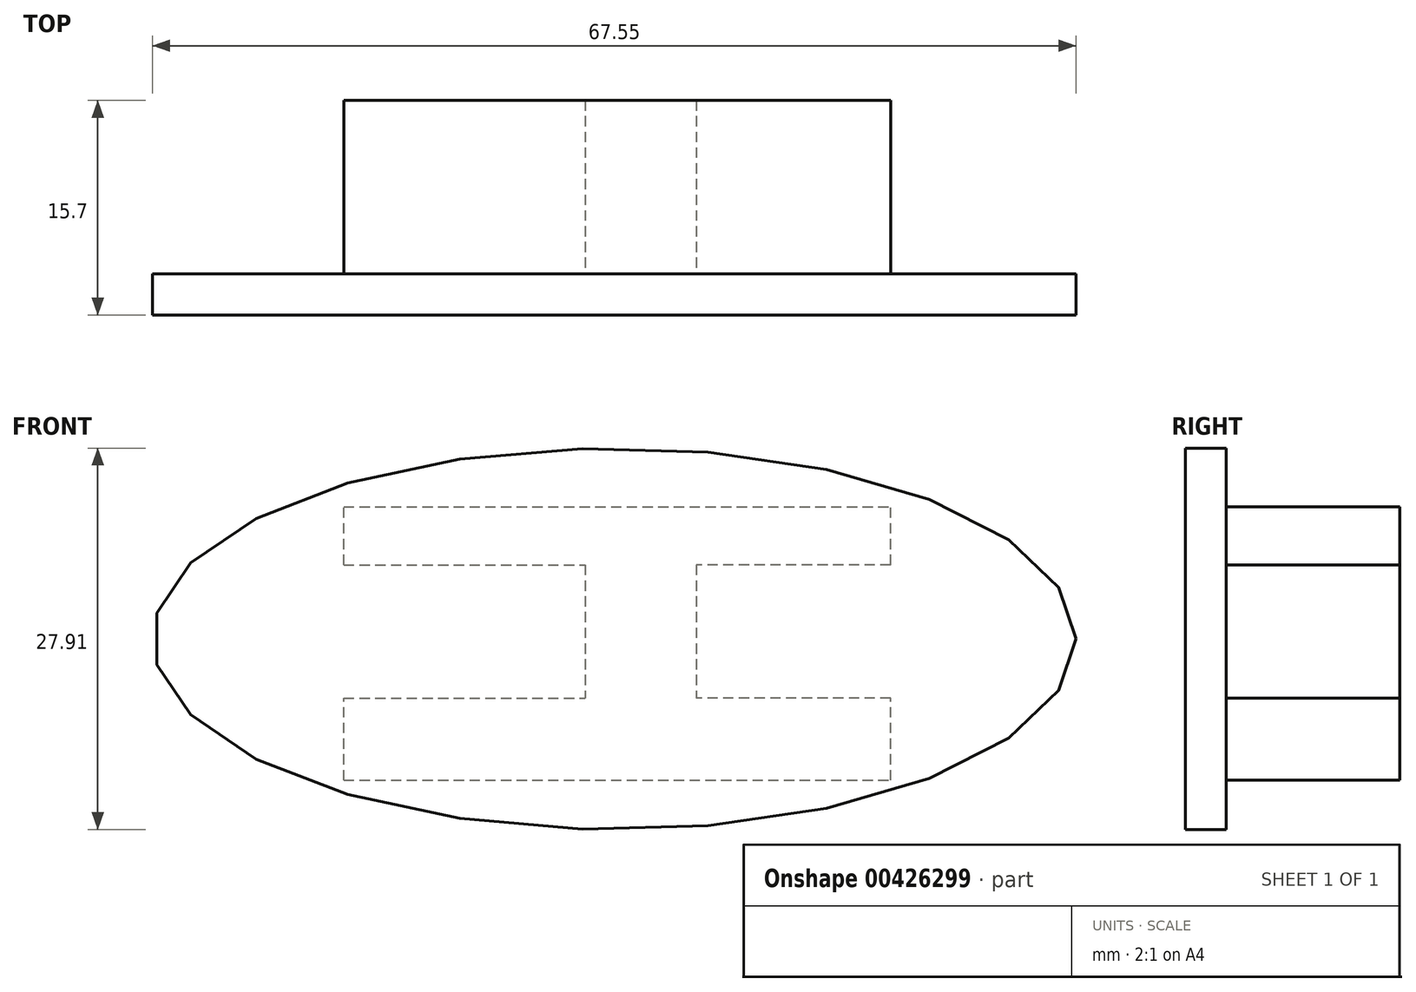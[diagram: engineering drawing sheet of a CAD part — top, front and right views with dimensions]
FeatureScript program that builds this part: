
annotation { "Feature Type Name" : "Feature", "Feature Type Description" : "" }
export const myFeature = defineFeature(function(context is Context, id is Id, definition is map)
    precondition{}
    {
        {
            var Q0;
            Q0=qCreatedBy(makeId("Front.planeOp"),FACE);
            var sketch = newSketch(context, id + "F0", { "sketchPlane" : qUnion([Q0])});
            skLineSegment(sketch, "E0.bottom", {"start": v(0, 0) * mm, "end": v(40, 0) * mm});
            skLineSegment(sketch, "E0.top", {"start": v(0, 20) * mm, "end": v(40, 20) * mm});
            skLineSegment(sketch, "E0.left", {"start": v(0, 0) * mm, "end": v(0, 6.02) * mm});
            skLineSegment(sketch, "E0.right", {"start": v(40, 0) * mm, "end": v(40, 6.02) * mm});
            skLineSegment(sketch, "E1.bottom", {"start": v(0, 15.76) * mm, "end": v(17.67, 15.76) * mm});
            skLineSegment(sketch, "E1.top", {"start": v(0, 6.02) * mm, "end": v(17.67, 6.02) * mm});
            skLineSegment(sketch, "E1.right", {"start": v(17.67, 15.76) * mm, "end": v(17.67, 6.02) * mm});
            skLineSegment(sketch, "E2.bottom", {"start": v(40, 15.76) * mm, "end": v(25.78, 15.76) * mm});
            skLineSegment(sketch, "E2.top", {"start": v(40, 6.02) * mm, "end": v(25.78, 6.02) * mm});
            skLineSegment(sketch, "E2.right", {"start": v(25.78, 15.76) * mm, "end": v(25.78, 6.02) * mm});
            skLineSegment(sketch, "E3.trimOffspring", {"start": v(0, 15.76) * mm, "end": v(0, 20) * mm});
            skLineSegment(sketch, "E4.trimOffspring", {"start": v(40, 15.76) * mm, "end": v(40, 20) * mm});
            skSolve(sketch);
        }
        {
            var Q0;
            Q0 = qSketchRegion(id + "F0", true);
            extrude(context, id + "F1", {"entities" : qUnion([Q0]), "oppositeDirection" : true, "depth" : 12.7 * mm});
        }
        {
            var Q0;
            Q0=qCreatedBy(makeId("Front.planeOp"),FACE);
            var sketch = newSketch(context, id + "F2", { "sketchPlane" : qUnion([Q0])});
            skEllipse(sketch, "E5", {"center": v(19.78, 10.34) * mm, "majorRadius": 33.77 * mm, "minorRadius": 13.95 * mm, "majorAxis": v(1, 0)});
            skSolve(sketch);
        }
        {
            var Q0;
            Q0 = qSketchRegion(id + "F2", true);
            extrude(context, id + "F3", {"entities" : qUnion([Q0]), "operationType" : NewBodyOperationType.ADD, "depth" : 3 * mm});
        }
    });
